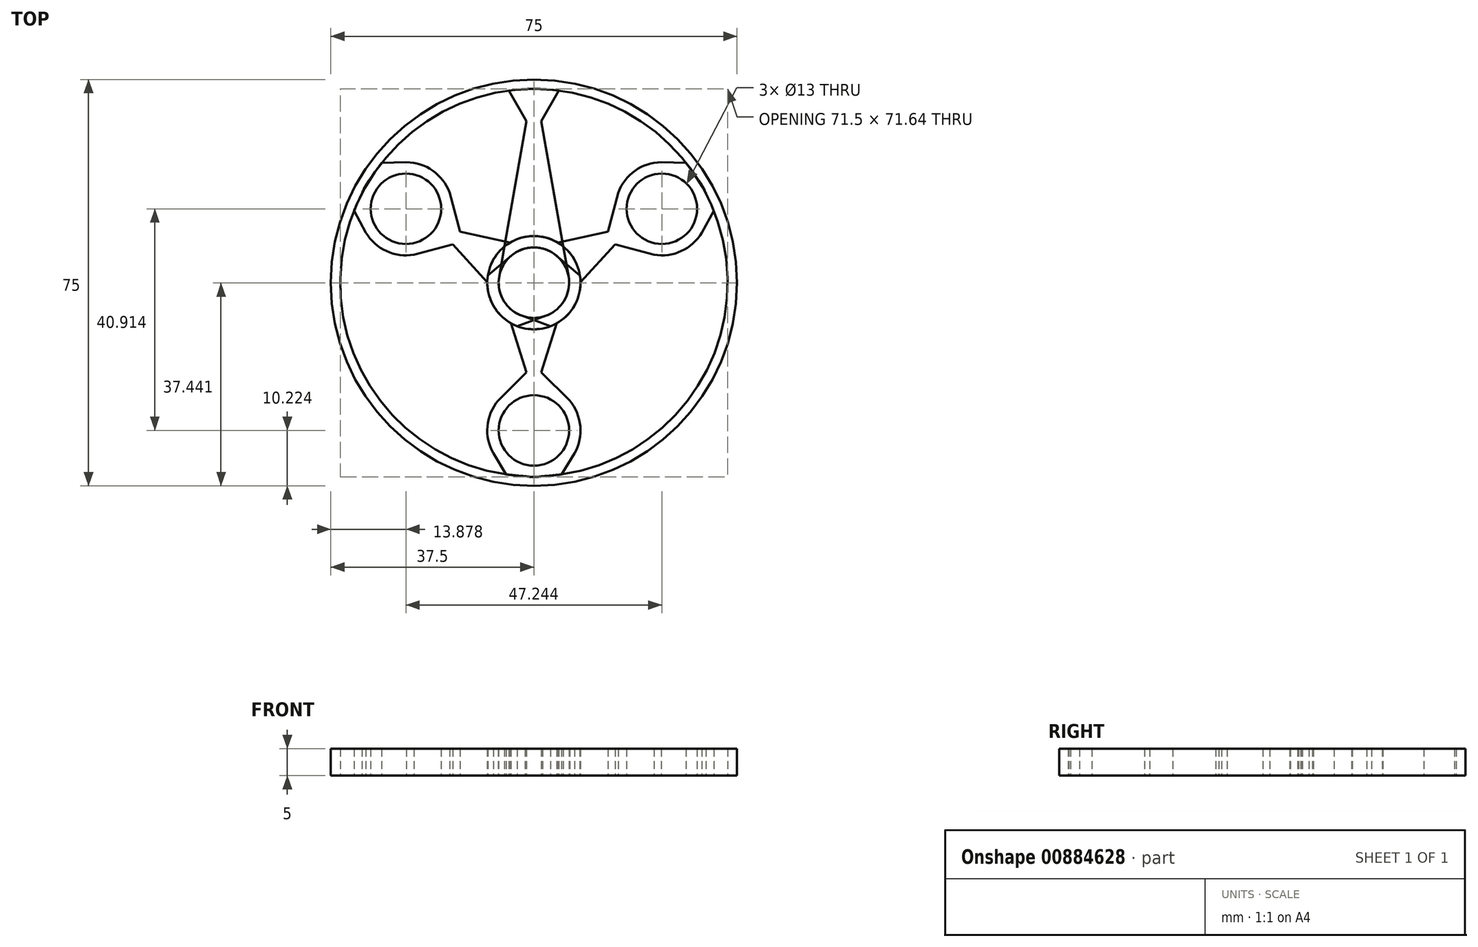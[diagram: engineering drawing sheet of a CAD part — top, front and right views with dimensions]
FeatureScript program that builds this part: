
annotation { "Feature Type Name" : "Feature", "Feature Type Description" : "" }
export const myFeature = defineFeature(function(context is Context, id is Id, definition is map)
    precondition{}
    {
        {
            var Q0;
            Q0=qCreatedBy(makeId("Top.planeOp"),FACE);
            var sketch = newSketch(context, id + "F0", { "sketchPlane" : qUnion([Q0])});
            skCircle(sketch, "E0", {"center": v(0, 0) * mm, "radius": 6.5 * mm});
            skLineSegment(sketch, "E1", {"start": v(0, 37.5) * mm, "end": v(-6.6, 0) * mm});
            skLineSegment(sketch, "E2", {"start": v(-6.6, 0) * mm, "end": v(0, 37.5) * mm});
            skLineSegment(sketch, "E3", {"start": v(0, 37.5) * mm, "end": v(6.6, 0) * mm});
            skPoint(sketch, "E4.startSnap0", {"position": v(-3.3, 18.75) * mm});
            skCircle(sketch, "E5", {"center": v(0, 0) * mm, "radius": 8.6 * mm});
            skCircle(sketch, "E6", {"center": v(0, 0) * mm, "radius": 35.76 * mm});
            skCircle(sketch, "E7", {"center": v(0, 0) * mm, "radius": 37.5 * mm});
            skCircle(sketch, "E8", {"center": v(0, -27.28) * mm, "radius": 8.6 * mm});
            skCircle(sketch, "E9", {"center": v(0, -27.28) * mm, "radius": 6.5 * mm});
            skLineSegment(sketch, "E10", {"start": v(-6.6, 0) * mm, "end": v(0, -20.78) * mm});
            skLineSegment(sketch, "E11", {"start": v(0, -20.78) * mm, "end": v(6.6, 0) * mm});
            skLineSegment(sketch, "E12", {"start": v(-6.6, -21.77) * mm, "end": v(0, -15.18) * mm});
            skLineSegment(sketch, "E13", {"start": v(0, -15.18) * mm, "end": v(6.61, -21.77) * mm});
            skLineSegment(sketch, "E14", {"start": v(-1.35, 29.8) * mm, "end": v(-4.62, 35.46) * mm});
            skLineSegment(sketch, "E15", {"start": v(-4.62, 35.46) * mm, "end": v(-1.35, 29.8) * mm});
            skLineSegment(sketch, "E16", {"start": v(-1.35, 29.8) * mm, "end": v(1.35, 29.8) * mm});
            skLineSegment(sketch, "E17", {"start": v(1.35, 29.8) * mm, "end": v(4.62, 35.46) * mm});
            skLineSegment(sketch, "E18", {"start": v(-7.5, -31.5) * mm, "end": v(-5.12, -35.4) * mm});
            skLineSegment(sketch, "E19", {"start": v(-5.12, -35.4) * mm, "end": v(-7.5, -31.5) * mm});
            skLineSegment(sketch, "E20", {"start": v(7.5, -31.5) * mm, "end": v(5.12, -35.4) * mm});
            skSolve(sketch);
        }
        {
            var Q0;
            {var subQ1=sQuery(id+"F0.wireOp",EDGE,"E2");var subQ3=sQuery(id+"F0.wireOp",EDGE,"E5");var subQ4=makeQuery(id+"F0.imprint","INTERSECT",VERTEX,{"derivedFrom":[subQ1,subQ3]});Q0=makeQuery(id+"F0.imprint","IMPRINT",FACE,{"disambiguationData":[TD([[makeQuery(id+"F0.imprint","IMPRINT",EDGE,{"disambiguationData":[TD([[subQ4,1.0]])],"derivedFrom":subQ3}),-1.0]])]});}
            var Q1;
            {var subQ0=sQuery(id+"F0.wireOp",EDGE,"E2");var subQ1=sQuery(id+"F0.wireOp",EDGE,"E0");var subQ2=makeQuery(id+"F0.imprint","INTERSECT",VERTEX,{"derivedFrom":[subQ1,subQ0]});Q1=makeQuery(id+"F0.imprint","IMPRINT",FACE,{"disambiguationData":[TD([[makeQuery(id+"F0.imprint","IMPRINT",EDGE,{"disambiguationData":[TD([[subQ2,-1.0]])],"derivedFrom":subQ1}),-1.0]])]});}
            var Q2;
            {var subQ0=sQuery(id+"F0.wireOp",EDGE,"E2");var subQ1=sQuery(id+"F0.wireOp",EDGE,"E0");var subQ2=makeQuery(id+"F0.imprint","INTERSECT",VERTEX,{"derivedFrom":[subQ1,subQ0]});Q2=makeQuery(id+"F0.imprint","IMPRINT",FACE,{"disambiguationData":[TD([[makeQuery(id+"F0.imprint","IMPRINT",EDGE,{"disambiguationData":[TD([[subQ2,1.0]])],"derivedFrom":subQ1}),-1.0]])]});}
            var Q3;
            Q3=makeQuery(id+"F0.imprint","IMPRINT",FACE,{"disambiguationData":[TD([[makeQuery(id+"F0.imprint","IMPRINT",EDGE,{"derivedFrom":sQuery(id+"F0.wireOp",EDGE,"E9")}),-1.0]])]});
            var Q4;
            {var subQ0=sQuery(id+"F0.wireOp",EDGE,"E8");var subQ1=sQuery(id+"F0.wireOp",EDGE,"E6");var subQ2=makeQuery(id+"F0.imprint","INTERSECT",VERTEX,{"disambiguationData":[OD(0.0)],"derivedFrom":[subQ1,subQ0]});Q4=makeQuery(id+"F0.imprint","IMPRINT",FACE,{"disambiguationData":[TD([[makeQuery(id+"F0.imprint","IMPRINT",EDGE,{"disambiguationData":[TD([[subQ2,-1.0]])],"derivedFrom":subQ1}),-1.0]])]});}
            var Q5;
            {var subQ0=sQuery(id+"F0.wireOp",EDGE,"E10");var subQ1=sQuery(id+"F0.wireOp",EDGE,"E5");var subQ2=makeQuery(id+"F0.imprint","INTERSECT",VERTEX,{"derivedFrom":[subQ1,subQ0]});Q5=makeQuery(id+"F0.imprint","IMPRINT",FACE,{"disambiguationData":[TD([[makeQuery(id+"F0.imprint","IMPRINT",EDGE,{"disambiguationData":[TD([[subQ2,-1.0]])],"derivedFrom":subQ1}),-1.0]])]});}
            var Q6;
            {var subQ0=sQuery(id+"F0.wireOp",EDGE,"E11");var subQ3=sQuery(id+"F0.wireOp",EDGE,"E0");var subQ5=makeQuery(id+"F0.imprint","INTERSECT",VERTEX,{"disambiguationData":[OD(0.0)],"derivedFrom":[subQ3,subQ0]});Q6=makeQuery(id+"F0.imprint","IMPRINT",FACE,{"disambiguationData":[TD([[makeQuery(id+"F0.imprint","IMPRINT",EDGE,{"disambiguationData":[TD([[subQ5,-1.0]])],"derivedFrom":subQ3}),-1.0]])]});}
            var Q7;
            {var subQ3=sQuery(id+"F0.wireOp",EDGE,"E10");var subQ6=sQuery(id+"F0.wireOp",EDGE,"E0");var subQ8=makeQuery(id+"F0.imprint","INTERSECT",VERTEX,{"disambiguationData":[OD(0.0)],"derivedFrom":[subQ6,subQ3]});Q7=makeQuery(id+"F0.imprint","IMPRINT",FACE,{"disambiguationData":[TD([[makeQuery(id+"F0.imprint","IMPRINT",EDGE,{"disambiguationData":[TD([[subQ8,-1.0]])],"derivedFrom":subQ6}),-1.0]])]});}
            var Q8;
            {var subQ0=sQuery(id+"F0.wireOp",EDGE,"E10");var subQ1=sQuery(id+"F0.wireOp",EDGE,"E8");var subQ2=makeQuery(id+"F0.imprint","INTERSECT",VERTEX,{"derivedFrom":[subQ1,subQ0]});Q8=makeQuery(id+"F0.imprint","IMPRINT",FACE,{"disambiguationData":[TD([[makeQuery(id+"F0.imprint","IMPRINT",EDGE,{"disambiguationData":[TD([[subQ2,1.0]])],"derivedFrom":subQ1}),1.0]])]});}
            var Q9;
            {var subQ0=sQuery(id+"F0.wireOp",EDGE,"E10");var subQ1=sQuery(id+"F0.wireOp",EDGE,"E0");var subQ2=makeQuery(id+"F0.imprint","INTERSECT",VERTEX,{"disambiguationData":[OD(1.0)],"derivedFrom":[subQ1,subQ0]});Q9=makeQuery(id+"F0.imprint","IMPRINT",FACE,{"disambiguationData":[TD([[makeQuery(id+"F0.imprint","IMPRINT",EDGE,{"disambiguationData":[TD([[subQ2,-1.0]])],"derivedFrom":subQ1}),-1.0]])]});}
            var Q10;
            {var subQ0=sQuery(id+"F0.wireOp",EDGE,"E11");var subQ1=sQuery(id+"F0.wireOp",EDGE,"E8");var subQ2=makeQuery(id+"F0.imprint","INTERSECT",VERTEX,{"derivedFrom":[subQ1,subQ0]});Q10=makeQuery(id+"F0.imprint","IMPRINT",FACE,{"disambiguationData":[TD([[makeQuery(id+"F0.imprint","IMPRINT",EDGE,{"disambiguationData":[TD([[subQ2,-1.0]])],"derivedFrom":subQ1}),-1.0]])]});}
            var Q11;
            {var subQ0=sQuery(id+"F0.wireOp",EDGE,"E10");var subQ1=sQuery(id+"F0.wireOp",EDGE,"E8");var subQ2=makeQuery(id+"F0.imprint","INTERSECT",VERTEX,{"derivedFrom":[subQ1,subQ0]});Q11=makeQuery(id+"F0.imprint","IMPRINT",FACE,{"disambiguationData":[TD([[makeQuery(id+"F0.imprint","IMPRINT",EDGE,{"disambiguationData":[TD([[subQ2,-1.0]])],"derivedFrom":subQ1}),-1.0]])]});}
            var Q12;
            {var subQ0=sQuery(id+"F0.wireOp",EDGE,"E13");var subQ1=sQuery(id+"F0.wireOp",EDGE,"E8");var subQ2=makeQuery(id+"F0.imprint","INTERSECT",VERTEX,{"disambiguationData":[OD(1.0)],"derivedFrom":[subQ1,subQ0]});Q12=makeQuery(id+"F0.imprint","IMPRINT",FACE,{"disambiguationData":[TD([[makeQuery(id+"F0.imprint","IMPRINT",EDGE,{"disambiguationData":[TD([[subQ2,-1.0]])],"derivedFrom":subQ1}),-1.0]])]});}
            var Q13;
            {var subQ0=sQuery(id+"F0.wireOp",EDGE,"E15");Q13=makeQuery(id+"F0.imprint","IMPRINT",FACE,{"disambiguationData":[TD([[makeQuery(id+"F0.imprint","IMPRINT",EDGE,{"derivedFrom":subQ0}),1.0]])]});}
            var Q14;
            {var subQ0=sQuery(id+"F0.wireOp",EDGE,"E16");Q14=makeQuery(id+"F0.imprint","IMPRINT",FACE,{"disambiguationData":[TD([[makeQuery(id+"F0.imprint","IMPRINT",EDGE,{"derivedFrom":subQ0}),1.0]])]});}
            var Q15;
            {var subQ0=sQuery(id+"F0.wireOp",EDGE,"E17");Q15=makeQuery(id+"F0.imprint","IMPRINT",FACE,{"disambiguationData":[TD([[makeQuery(id+"F0.imprint","IMPRINT",EDGE,{"derivedFrom":subQ0}),1.0]])]});}
            var Q16;
            {var subQ0=sQuery(id+"F0.wireOp",EDGE,"E19");var subQ1=sQuery(id+"F0.wireOp",EDGE,"E6");var subQ2=makeQuery(id+"F0.imprint","INTERSECT",VERTEX,{"derivedFrom":[subQ1,subQ0]});Q16=makeQuery(id+"F0.imprint","IMPRINT",FACE,{"disambiguationData":[TD([[makeQuery(id+"F0.imprint","IMPRINT",EDGE,{"disambiguationData":[TD([[subQ2,-1.0]])],"derivedFrom":subQ1}),1.0]])]});}
            var Q17;
            {var subQ0=sQuery(id+"F0.wireOp",EDGE,"E20");var subQ1=sQuery(id+"F0.wireOp",EDGE,"E6");var subQ2=makeQuery(id+"F0.imprint","INTERSECT",VERTEX,{"derivedFrom":[subQ1,subQ0]});Q17=makeQuery(id+"F0.imprint","IMPRINT",FACE,{"disambiguationData":[TD([[makeQuery(id+"F0.imprint","IMPRINT",EDGE,{"disambiguationData":[TD([[subQ2,1.0]])],"derivedFrom":subQ1}),1.0]])]});}
            extrude(context, id + "F1", {"entities" : qUnion([Q0, Q1, Q2, Q3, Q4, Q5, Q6, Q7, Q8, Q9, Q10, Q11, Q12, Q13, Q14, Q15, Q16, Q17]), "depth" : 5 * mm, "offsetDistance" : 25 * mm});
        }
        {
            var Q0;
            Q0=makeQuery(id+"F1.opExtrude","SWEPT_BODY",BODY,{"disambiguationData":[OSD([sQuery(id+"F0.wireOp",EDGE,"E0"),sQuery(id+"F0.wireOp",EDGE,"E2"),sQuery(id+"F0.wireOp",EDGE,"E3"),sQuery(id+"F0.wireOp",EDGE,"E5")])]});
            var Q1;
            Q1=makeQuery(id+"F1.opExtrude","SWEPT_BODY",BODY,{"disambiguationData":[OSD([sQuery(id+"F0.wireOp",EDGE,"E8"),sQuery(id+"F0.wireOp",EDGE,"E9")])]});
            var Q2;
            {var subQ0=sQuery(id+"F0.wireOp",EDGE,"E5");Q2=makeQuery(id+"F1.opExtrude","SWEPT_FACE",FACE,{"disambiguationData":[OSD([subQ0]),TDD([makeQuery(id+"F0.imprint","IMPRINT",EDGE,{"disambiguationData":[TD([[makeQuery(id+"F0.imprint","INTERSECT",VERTEX,{"derivedFrom":[sQuery(id+"F0.wireOp",EDGE,"E3"),subQ0]}),1.0]])],"derivedFrom":subQ0})])]});}
            circularPattern(context, id + "F2", {"entities" : qUnion([Q0, Q1]), "axis" : qUnion([Q2]), "angle" : 360 * degree, "instanceCount" : 3, "equalSpace" : true});
        }
        {
            var Q0;
            Q0=qSketchRegion(id+"F0",true);
            extrude(context, id + "F3", {"entities" : qUnion([Q0]), "depth" : 5 * mm, "offsetDistance" : 25 * mm});
        }
    });
